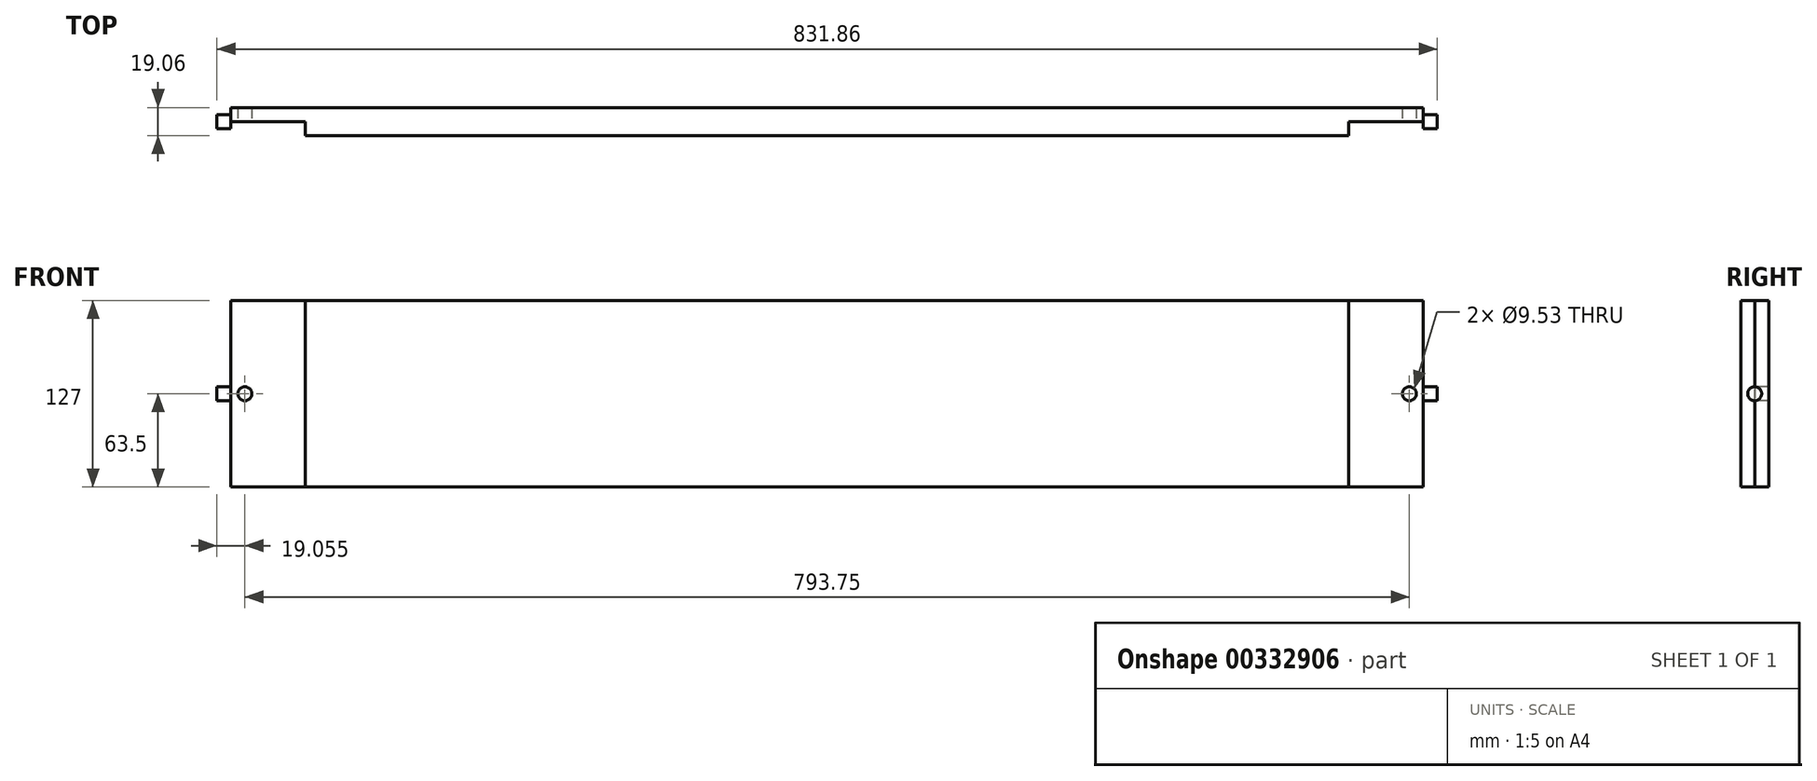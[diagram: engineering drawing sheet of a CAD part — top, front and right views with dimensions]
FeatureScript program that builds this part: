
annotation { "Feature Type Name" : "Feature", "Feature Type Description" : "" }
export const myFeature = defineFeature(function(context is Context, id is Id, definition is map)
    precondition{}
    {
        {
            var Q0;
            Q0=qCreatedBy(makeId("Top.planeOp"),FACE);
            var sketch = newSketch(context, id + "F0", { "sketchPlane" : qUnion([Q0])});
            skLineSegment(sketch, "E0.bottom", {"start": v(-355.6, -9.52) * mm, "end": v(355.6, -9.52) * mm});
            skLineSegment(sketch, "E0.top", {"start": v(-406.4, 9.53) * mm, "end": v(406.4, 9.53) * mm});
            skLineSegment(sketch, "E0.left", {"start": v(-406.4, 0) * mm, "end": v(-406.4, 9.52) * mm});
            skLineSegment(sketch, "E0.right", {"start": v(406.4, 0) * mm, "end": v(406.4, 9.52) * mm});
            skPoint(sketch, "E0.middle", {"position": v(0, 0) * mm});
            skLineSegment(sketch, "E1.bottom", {"start": v(-406.4, 0) * mm, "end": v(-355.6, 0) * mm});
            skLineSegment(sketch, "E1.right", {"start": v(-355.6, 0) * mm, "end": v(-355.6, -9.52) * mm});
            skPoint(sketch, "E2.firstSnap0", {"position": v(406.4, 0) * mm});
            skLineSegment(sketch, "E2.bottom", {"start": v(355.6, 0) * mm, "end": v(406.4, 0) * mm});
            skLineSegment(sketch, "E2.left", {"start": v(355.6, 0) * mm, "end": v(355.6, -9.52) * mm});
            skPoint(sketch, "E1.top.end.orphan", {"position": v(-355.6, -21.73) * mm});
            skPoint(sketch, "E3.orphan", {"position": v(-148.04, 0) * mm});
            skPoint(sketch, "E4.orphan", {"position": v(-406.4, -9.52) * mm});
            skPoint(sketch, "E5.orphan", {"position": v(406.4, -9.52) * mm});
            skPoint(sketch, "E2.right.end.orphan", {"position": v(-107.65, -21.73) * mm});
            skSolve(sketch);
        }
        {
            var Q0;
            Q0=qSketchRegion(id+"F0",true);
            extrude(context, id + "F1", {"entities" : qUnion([Q0]), "depth" : 127 * mm});
        }
        {
            var Q0;
            Q0=qCreatedBy(makeId("Right.planeOp"),FACE);
            cPlane(context, id + "F2", {"entities" : qUnion([Q0]), "cplaneType" : CPlaneType.OFFSET, "offset" : 406.4 * mm, "width" : 152.4 * mm, "height" : 152.4 * mm});
        }
        {
            var Q0;
            Q0=qCreatedBy(id+"F2.planeOp",FACE);
            var sketch = newSketch(context, id + "F3", { "sketchPlane" : qUnion([Q0])});
            skCircle(sketch, "E6", {"center": v(0, 63.5) * mm, "radius": 4.76 * mm});
            skSolve(sketch);
        }
        {
            var Q0;
            Q0=qSketchRegion(id+"F3",true);
            extrude(context, id + "F4", {"entities" : qUnion([Q0]), "operationType" : NewBodyOperationType.ADD, "depth" : 9.52 * mm});
        }
        {
            var Q0;
            Q0=qCreatedBy(makeId("Right.planeOp"),FACE);
            cPlane(context, id + "F5", {"entities" : qUnion([Q0]), "cplaneType" : CPlaneType.OFFSET, "offset" : 406.4 * mm, "oppositeDirection" : true, "width" : 152.4 * mm, "height" : 152.4 * mm});
        }
        {
            var Q0;
            Q0=qCreatedBy(id+"F5.planeOp",FACE);
            var sketch = newSketch(context, id + "F6", { "sketchPlane" : qUnion([Q0])});
            skCircle(sketch, "E7", {"center": v(0, 63.5) * mm, "radius": 4.76 * mm});
            skSolve(sketch);
        }
        {
            var Q0;
            Q0=qSketchRegion(id+"F6",true);
            extrude(context, id + "F7", {"entities" : qUnion([Q0]), "operationType" : NewBodyOperationType.ADD, "oppositeDirection" : true, "depth" : 9.52 * mm});
        }
        {
            var Q0;
            Q0=qCreatedBy(makeId("Front.planeOp"),FACE);
            var sketch = newSketch(context, id + "F8", { "sketchPlane" : qUnion([Q0])});
            skCircle(sketch, "E8", {"center": v(396.88, 63.5) * mm, "radius": 4.76 * mm});
            skCircle(sketch, "E9", {"center": v(-396.88, 63.5) * mm, "radius": 4.76 * mm});
            skSolve(sketch);
        }
        {
            var Q0;
            Q0 = qSketchRegion(id + "F8", true);
            extrude(context, id + "F9", {"entities" : qUnion([Q0]), "operationType" : NewBodyOperationType.REMOVE, "oppositeDirection" : true, "depth" : 25.4 * mm});
        }
    });
